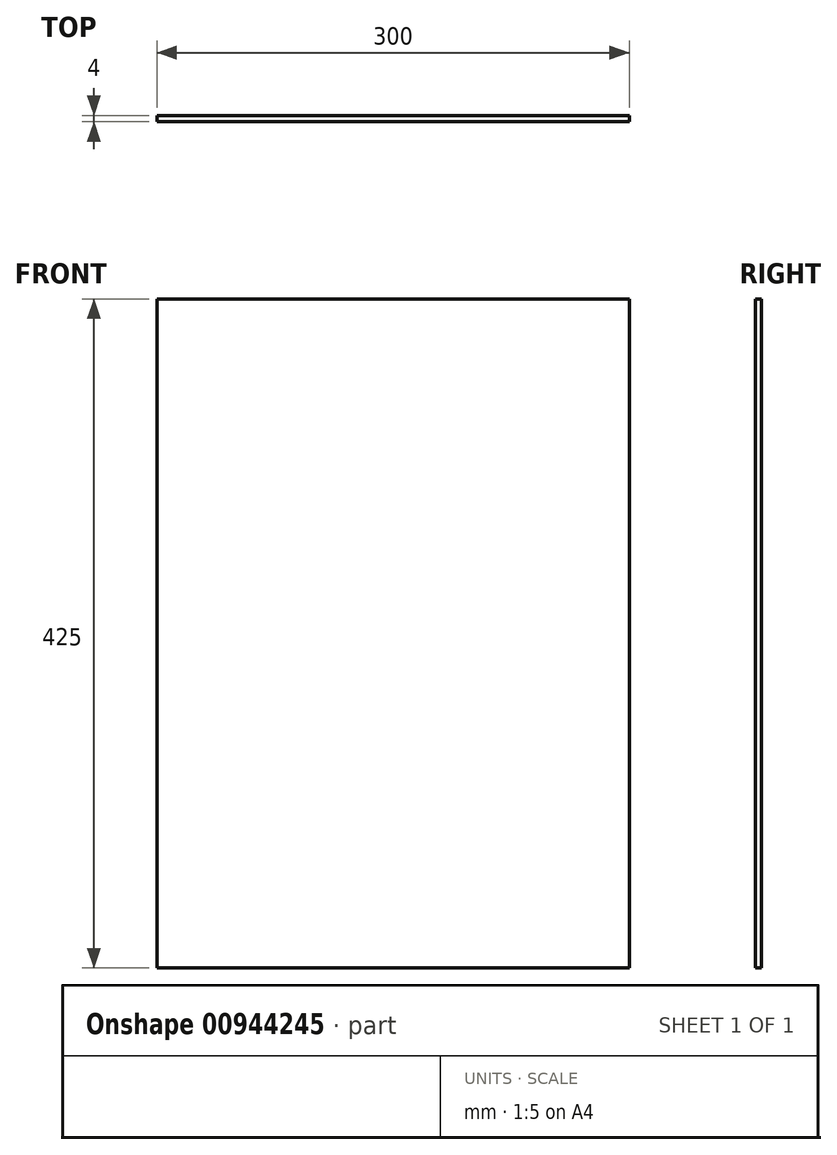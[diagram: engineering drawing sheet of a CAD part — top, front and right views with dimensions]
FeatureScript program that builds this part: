
annotation { "Feature Type Name" : "Feature", "Feature Type Description" : "" }
export const myFeature = defineFeature(function(context is Context, id is Id, definition is map)
    precondition{}
    {
        {
            var Q0;
            Q0=qCreatedBy(makeId("Front.planeOp"),FACE);
            var sketch = newSketch(context, id + "F0", { "sketchPlane" : qUnion([Q0])});
            skLineSegment(sketch, "E0.bottom", {"start": v(150, 212.5) * mm, "end": v(-150, 212.5) * mm});
            skLineSegment(sketch, "E0.top", {"start": v(150, -212.5) * mm, "end": v(-150, -212.5) * mm});
            skLineSegment(sketch, "E0.left", {"start": v(150, 212.5) * mm, "end": v(150, -212.5) * mm});
            skLineSegment(sketch, "E0.right", {"start": v(-150, 212.5) * mm, "end": v(-150, -212.5) * mm});
            skPoint(sketch, "E0.middle", {"position": v(0, 0) * mm});
            skSolve(sketch);
        }
        {
            var Q0;
            Q0 = qSketchRegion(id + "F0", true);
            extrude(context, id + "F1", {"entities" : qUnion([Q0]), "depth" : 4 * mm, "offsetDistance" : 25 * mm});
        }
    });
